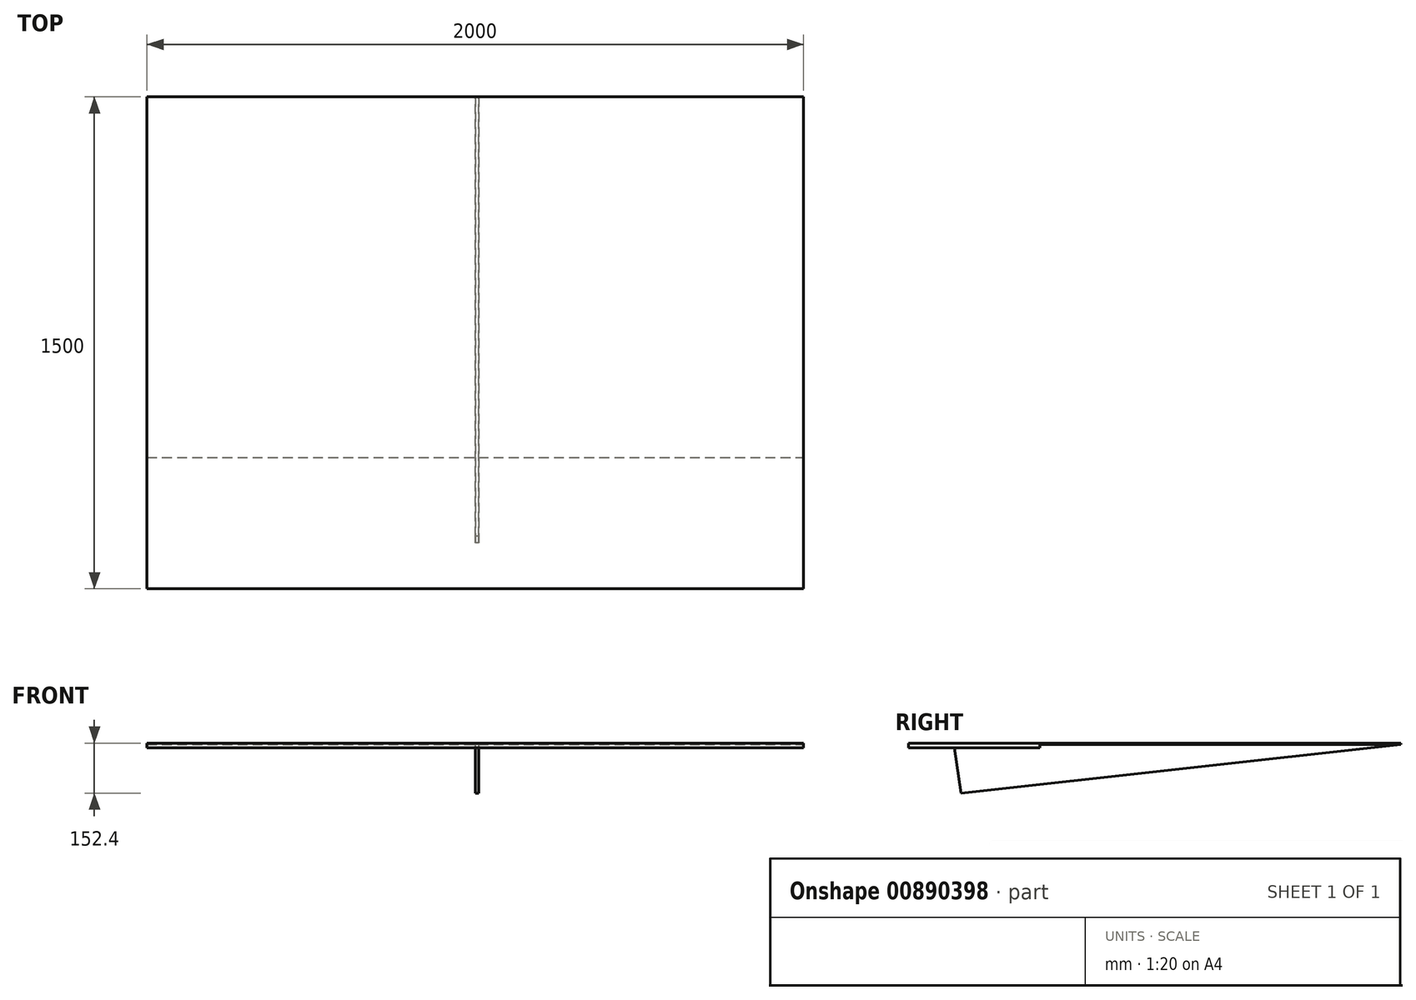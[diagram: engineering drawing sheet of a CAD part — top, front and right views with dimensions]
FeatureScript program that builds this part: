
annotation { "Feature Type Name" : "Feature", "Feature Type Description" : "" }
export const myFeature = defineFeature(function(context is Context, id is Id, definition is map)
    precondition{}
    {
        {
            var Q0;
            Q0=qCreatedBy(makeId("Top.planeOp"),FACE);
            var sketch = newSketch(context, id + "F0", { "sketchPlane" : qUnion([Q0])});
            skLineSegment(sketch, "E0.bottom", {"start": v(-1000, 500) * mm, "end": v(1000, 500) * mm});
            skLineSegment(sketch, "E0.top", {"start": v(-1000, -1000) * mm, "end": v(1000, -1000) * mm});
            skLineSegment(sketch, "E0.left", {"start": v(-1000, 500) * mm, "end": v(-1000, -1000) * mm});
            skLineSegment(sketch, "E0.right", {"start": v(1000, 500) * mm, "end": v(1000, -1000) * mm});
            skSolve(sketch);
        }
        {
            var Q0;
            Q0=makeQuery(id+"F0.imprint","IMPRINT",FACE,{"disambiguationData":[TD([[makeQuery(id+"F0.imprint","IMPRINT",EDGE,{"derivedFrom":sQuery(id+"F0.wireOp",EDGE,"E0.bottom")}),-1.0]])]});
            extrude(context, id + "F1", {"entities" : qUnion([Q0]), "oppositeDirection" : true, "depth" : 5 * mm, "offsetDistance" : 25 * mm});
        }
        {
            var Q0;
            Q0=makeQuery(id+"F1.opExtrude","CAP_FACE",FACE,{"disambiguationData":[OSD([sQuery(id+"F0.wireOp",EDGE,"E0.bottom"),sQuery(id+"F0.wireOp",EDGE,"E0.top"),sQuery(id+"F0.wireOp",EDGE,"E0.left"),sQuery(id+"F0.wireOp",EDGE,"E0.right")])],"isStart":false});
            var sketch = newSketch(context, id + "F2", { "sketchPlane" : qUnion([Q0])});
            skLineSegment(sketch, "E1.bottom", {"start": v(-1000, 1000) * mm, "end": v(1000, 1000) * mm});
            skLineSegment(sketch, "E1.top", {"start": v(-1000, 600) * mm, "end": v(1000, 600) * mm});
            skLineSegment(sketch, "E1.left", {"start": v(-1000, 1000) * mm, "end": v(-1000, 600) * mm});
            skLineSegment(sketch, "E1.right", {"start": v(1000, 1000) * mm, "end": v(1000, 600) * mm});
            skSolve(sketch);
        }
        {
            var Q0;
            Q0=makeQuery(id+"F2.imprint","IMPRINT",FACE,{"disambiguationData":[TD([[makeQuery(id+"F2.imprint","IMPRINT",EDGE,{"derivedFrom":sQuery(id+"F2.wireOp",EDGE,"E1.bottom")}),-1.0]])]});
            extrude(context, id + "F3", {"entities" : qUnion([Q0]), "operationType" : NewBodyOperationType.ADD, "depth" : 10 * mm, "offsetDistance" : 25 * mm});
        }
        {
            var Q0;
            Q0=qCreatedBy(makeId("Right.planeOp"),FACE);
            var sketch = newSketch(context, id + "F4", { "sketchPlane" : qUnion([Q0])});
            skLineSegment(sketch, "E2", {"start": v(-860, -15) * mm, "end": v(-840, -152.4) * mm});
            skLineSegment(sketch, "E3", {"start": v(-840, -152.4) * mm, "end": v(500, -5) * mm});
            skLineSegment(sketch, "E4", {"start": v(500, -5) * mm, "end": v(-600, -5) * mm});
            skLineSegment(sketch, "E5", {"start": v(-600, -5) * mm, "end": v(-600, -15) * mm});
            skLineSegment(sketch, "E6", {"start": v(-600, -15) * mm, "end": v(-860, -15) * mm});
            skSolve(sketch);
        }
        {
            var Q0;
            Q0=makeQuery(id+"F4.imprint","IMPRINT",FACE,{"disambiguationData":[TD([[makeQuery(id+"F4.imprint","IMPRINT",EDGE,{"derivedFrom":sQuery(id+"F4.wireOp",EDGE,"E2")}),1.0]])]});
            extrude(context, id + "F5", {"entities" : qUnion([Q0]), "operationType" : NewBodyOperationType.ADD, "depth" : 10 * mm, "offsetDistance" : 25 * mm});
        }
    });
